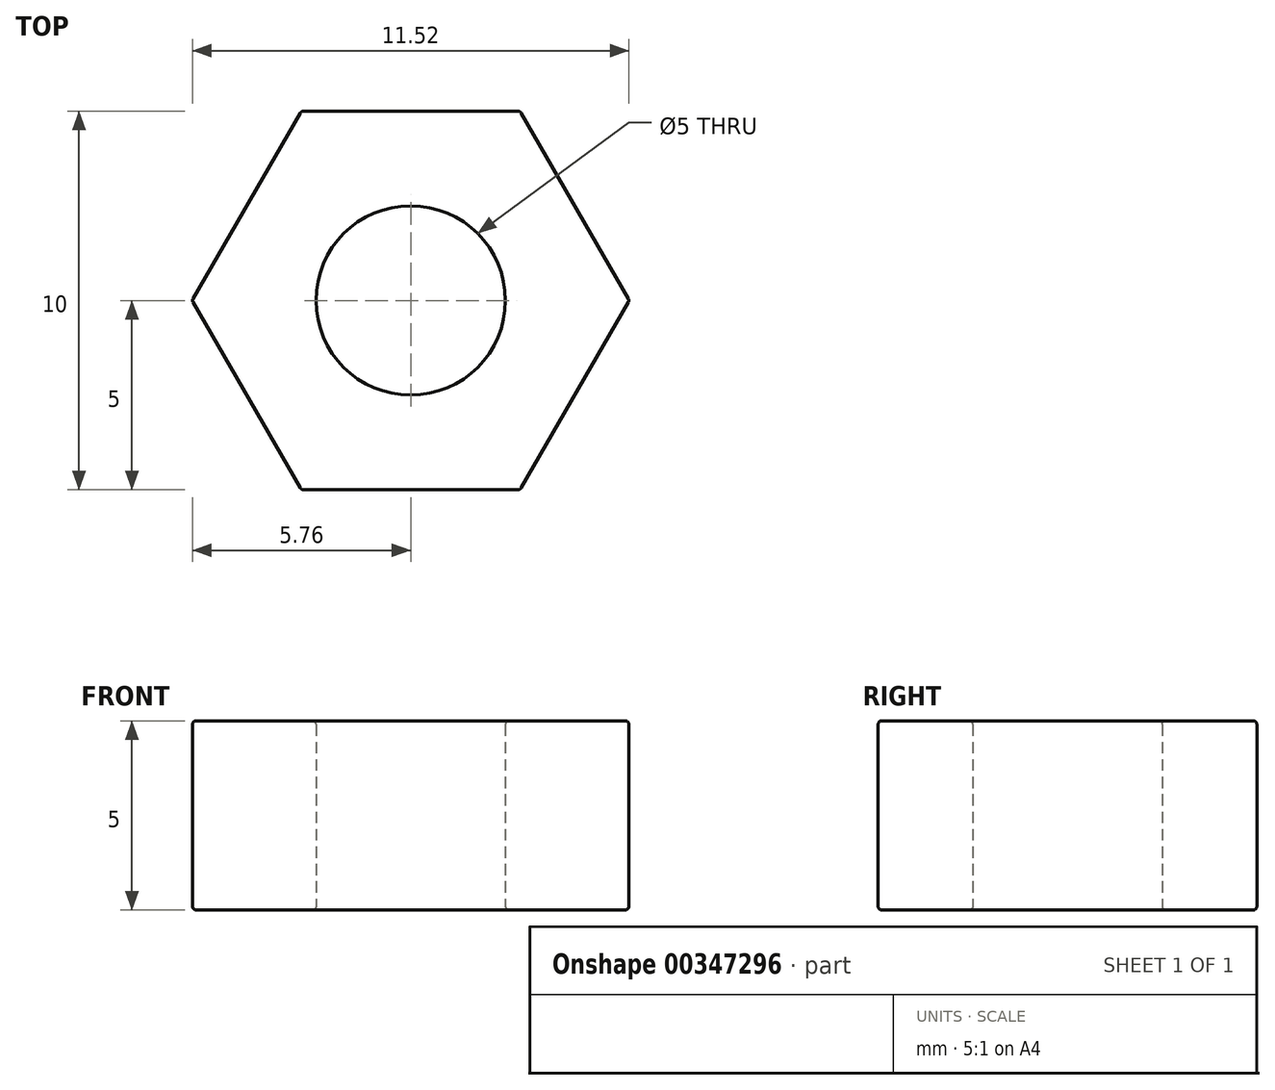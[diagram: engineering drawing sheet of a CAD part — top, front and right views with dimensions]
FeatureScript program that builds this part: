
annotation { "Feature Type Name" : "Feature", "Feature Type Description" : "" }
export const myFeature = defineFeature(function(context is Context, id is Id, definition is map)
    precondition{}
    {
        {
            var Q0;
            Q0=qCreatedBy(makeId("Top.planeOp"),FACE);
            var sketch = newSketch(context, id + "F0", { "sketchPlane" : qUnion([Q0])});
            skCircle(sketch, "E0.cCircle", {"center": v(0, 0) * mm, "radius": 5 * mm, "construction": true});
            skLineSegment(sketch, "E0.0", {"start": v(-2.89, -5) * mm, "end": v(-5.77, 0) * mm});
            skLineSegment(sketch, "E0.1", {"start": v(-5.77, 0) * mm, "end": v(-2.89, 5) * mm});
            skLineSegment(sketch, "E0.2", {"start": v(-2.89, 5) * mm, "end": v(2.89, 5) * mm});
            skLineSegment(sketch, "E0.3", {"start": v(2.89, 5) * mm, "end": v(5.77, 0) * mm});
            skLineSegment(sketch, "E0.4", {"start": v(5.77, 0) * mm, "end": v(2.89, -5) * mm});
            skLineSegment(sketch, "E0.5", {"start": v(2.89, -5) * mm, "end": v(-2.89, -5) * mm});
            skPoint(sketch, "E0.0.midPoint", {"position": v(-4.33, -2.5) * mm});
            skCircle(sketch, "E1", {"center": v(0, 0) * mm, "radius": 2.5 * mm});
            skSolve(sketch);
        }
        {
            var Q0;
            Q0 = qSketchRegion(id + "F0", true);
            extrude(context, id + "F1", {"entities" : qUnion([Q0]), "depth" : 5 * mm});
        }
        {
            var Q0;
            Q0=makeQuery(id+"F1.opExtrude","CAP_EDGE",EDGE,{"disambiguationData":[OSD([sQuery(id+"F0.wireOp",EDGE,"E0.2")])],"isStart":false});
            var Q1;
            Q1=makeQuery(id+"F1.opExtrude","CAP_EDGE",EDGE,{"disambiguationData":[OSD([sQuery(id+"F0.wireOp",EDGE,"E0.3")])],"isStart":false});
            var Q2;
            Q2=makeQuery(id+"F1.opExtrude","CAP_EDGE",EDGE,{"disambiguationData":[OSD([sQuery(id+"F0.wireOp",EDGE,"E0.4")])],"isStart":false});
            var Q3;
            Q3=makeQuery(id+"F1.opExtrude","CAP_EDGE",EDGE,{"disambiguationData":[OSD([sQuery(id+"F0.wireOp",EDGE,"E0.5")])],"isStart":false});
            var Q4;
            Q4=makeQuery(id+"F1.opExtrude","CAP_EDGE",EDGE,{"disambiguationData":[OSD([sQuery(id+"F0.wireOp",EDGE,"E0.0")])],"isStart":false});
            var Q5;
            Q5=makeQuery(id+"F1.opExtrude","CAP_EDGE",EDGE,{"disambiguationData":[OSD([sQuery(id+"F0.wireOp",EDGE,"E0.1")])],"isStart":false});
            var Q6;
            Q6=makeQuery(id+"F1.opExtrude","SWEPT_FACE",FACE,{"disambiguationData":[OSD([sQuery(id+"F0.wireOp",EDGE,"E0.5")])]});
            var Q7;
            Q7=makeQuery(id+"F1.opExtrude","SWEPT_FACE",FACE,{"disambiguationData":[OSD([sQuery(id+"F0.wireOp",EDGE,"E0.4")])]});
            var Q8;
            Q8=makeQuery(id+"F1.opExtrude","CAP_EDGE",EDGE,{"disambiguationData":[OSD([sQuery(id+"F0.wireOp",EDGE,"E1")])],"isStart":false});
            var Q9;
            Q9=makeQuery(id+"F1.opExtrude","CAP_EDGE",EDGE,{"disambiguationData":[OSD([sQuery(id+"F0.wireOp",EDGE,"E0.0")])],"isStart":true});
            var Q10;
            Q10=makeQuery(id+"F1.opExtrude","SWEPT_EDGE",EDGE,{"disambiguationData":[OSD([sQuery(id+"F0.wireOp",EDGE,"E0.0"),sQuery(id+"F0.wireOp",EDGE,"E0.1")])]});
            var Q11;
            Q11=makeQuery(id+"F1.opExtrude","CAP_FACE",FACE,{"disambiguationData":[OSD([sQuery(id+"F0.wireOp",EDGE,"E0.0"),sQuery(id+"F0.wireOp",EDGE,"E0.1"),sQuery(id+"F0.wireOp",EDGE,"E0.2"),sQuery(id+"F0.wireOp",EDGE,"E0.3"),sQuery(id+"F0.wireOp",EDGE,"E0.4"),sQuery(id+"F0.wireOp",EDGE,"E0.5"),sQuery(id+"F0.wireOp",EDGE,"E1")])],"isStart":true});
            var Q12;
            Q12=makeQuery(id+"F1.opExtrude","SWEPT_FACE",FACE,{"disambiguationData":[OSD([sQuery(id+"F0.wireOp",EDGE,"E0.2")])]});
            fillet(context, id + "F2", {"entities" : qUnion([Q0, Q1, Q2, Q3, Q4, Q5, Q6, Q7, Q8, Q9, Q10, Q11, Q12]), "radius" : 0.1 * mm, "tangentPropagation" : true, "allowEdgeOverflow" : false});
        }
    });
